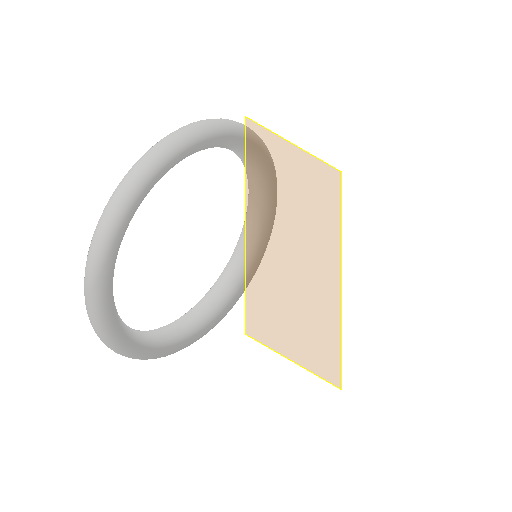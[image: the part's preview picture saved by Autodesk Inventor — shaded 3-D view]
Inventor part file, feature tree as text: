
AUTODESK INVENTOR PART (.ipt)
format: ipt  version: 2023 (Build 270158000, 158)  size: 124,416 bytes
history: native  units: mm
features: plane x1, revolve x1, sketch x1
ambient origin geometry x8: Origin, YZ Plane, XZ Plane, XY Plane, X Axis, Y Axis, Z Axis, Center Point
bodies: Volumenkörper1 (feature_tree)
feature tree (3):
  plane  "Arbeitsebene1"
  revolve  "Umdrehung1"
  sketch  "Skizze1"  dims[d0=3.0mm d1=12.0mm d2=90.0deg]
